# Revit family: Doors-Sliding_WON-DOOR_DuraSound_Motorized_Floating_N
name_source: partatom
category: Doors
units: mm (PartAtom-declared; Revit-internal decimal feet)

## family parameters
Always vertical = Yes
Cut with Voids When Loaded = No
Host = Wall
OmniClass Number = 23.17.11.37.13
OmniClass Title = Sound Control Doors
Room Calculation Point = No
Shared = No

## types (2) — shared parameters
Description = Won-Door DuraSound accordion folding doors increase building utility by performing multiple functions. These versatile accordion partitions are competitively priced, cost less to install and maintain, and last years longer than any other folding partition on the market.The dual-wall DuraSound accordion folding partition has the highest sound rating (STC 48  or equivalent NIC 30 ) in the industry. Each steel panel is corrugated for extra strength. Surface colors and vinyl finishes are permanently bonded. The result is a partition that is dent, ding and scratch resistant. DuraSound doors are only 4.2 pounds per square foot – and operate on a two-track system. A pin and roller suspends every panel and promotes smooth and low effort operation. This unique design allows the doors to span large, as well as curved, openings.  Available in unlimited widths, and heights up to 28 feet.
Door Finish = Won-Door-Plastic-Vinyl
Manufacturer = Won-Door Corporation
Model = DS Motorized Floating
Offset = 0' - 0"
Offset for Backing Depth = 0' - 6 1/8"
Offset for Backing Width = 0' - 3 1/8"
Offset for Stack Depth = 0' - 4 7/8"
Pocket Thickness = 2' - 3 3/4"
Product Page URL = https://www.wondoor.com
Product data url = https://bimobject.com
Real Thickness = 0' - 11 3/4"
Thickness = 1' - 0 5/8"
URL = https://www.wondoor.com
Version = 1
Wall Closure = By host

## per-type parameters (varying)
| type | Double Door | Single Door |
| Single Parting Door | No | Yes |
| Bi-Parting Door | Yes | No |

## geometry (parser evidence)
native form markers: Sweep x13
no freeform markers — native parametric forms only
